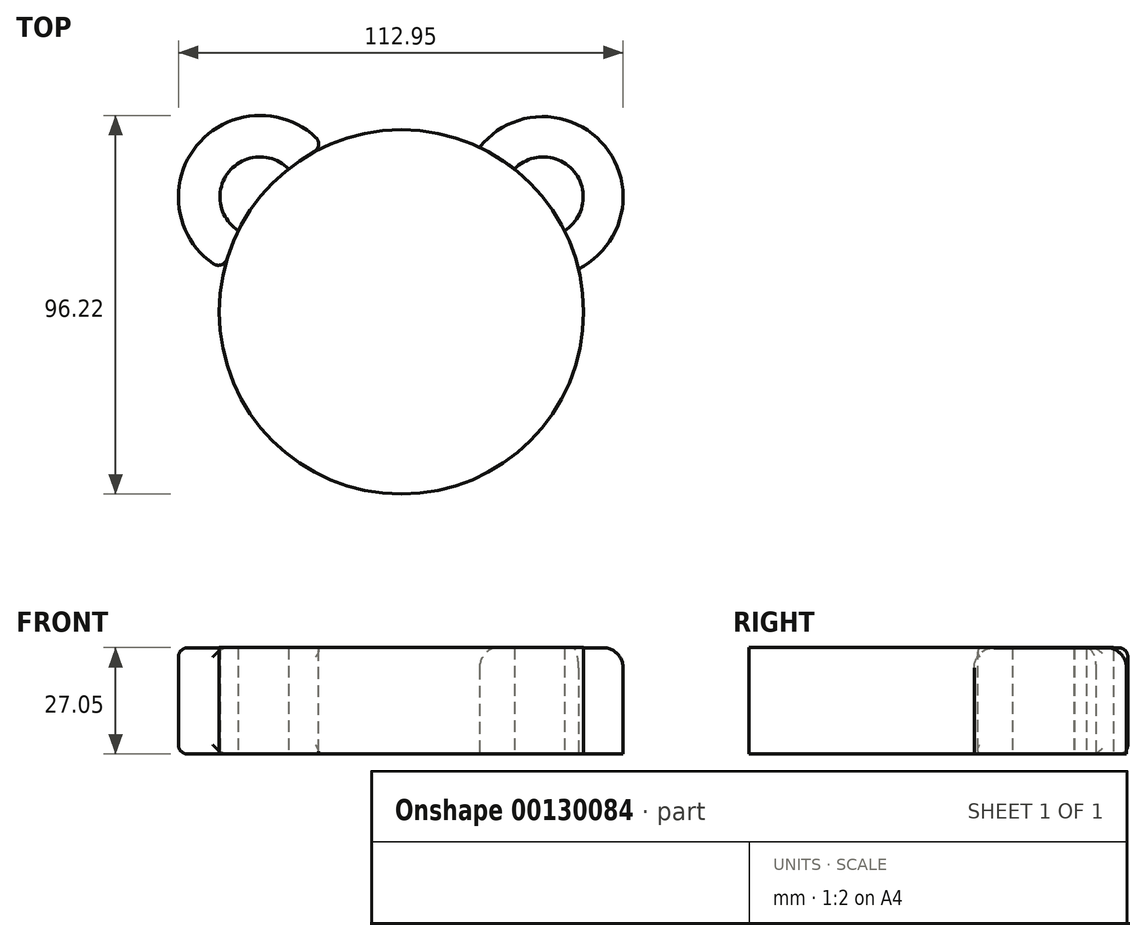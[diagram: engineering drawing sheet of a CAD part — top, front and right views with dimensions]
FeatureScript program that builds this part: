
annotation { "Feature Type Name" : "Feature", "Feature Type Description" : "" }
export const myFeature = defineFeature(function(context is Context, id is Id, definition is map)
    precondition{}
    {
        {
            var Q0;
            Q0=qCreatedBy(makeId("Top.planeOp"),FACE);
            var sketch = newSketch(context, id + "F0", { "sketchPlane" : qUnion([Q0])});
            skCircle(sketch, "E0", {"center": v(0, 0) * mm, "radius": 46.3 * mm});
            skArc(sketch, "E1", {"start": v(-19.58, 41.95) * mm, "mid": v(-51.99, 42.28) * mm, "end": v(-45.06, 10.62) * mm});
            skArc(sketch, "E2", {"start": v(44.98, 10.93) * mm, "mid": v(51.75, 42.09) * mm, "end": v(19.86, 41.81) * mm});
            skArc(sketch, "E3", {"start": v(-28.67, 36.35) * mm, "mid": v(-43.8, 35.62) * mm, "end": v(-41.42, 20.67) * mm});
            skArc(sketch, "E4", {"start": v(41.45, 20.61) * mm, "mid": v(43.92, 35.61) * mm, "end": v(28.73, 36.3) * mm});
            skSolve(sketch);
        }
        {
            var Q0;
            {var subQ0=sQuery(id+"F0.wireOp",EDGE,"E1");Q0=makeQuery(id+"F0.imprint","IMPRINT",FACE,{"disambiguationData":[TD([[makeQuery(id+"F0.imprint","IMPRINT",EDGE,{"derivedFrom":subQ0}),1.0]])]});}
            var Q1;
            {var subQ0=sQuery(id+"F0.wireOp",EDGE,"E2");Q1=makeQuery(id+"F0.imprint","IMPRINT",FACE,{"disambiguationData":[TD([[makeQuery(id+"F0.imprint","IMPRINT",EDGE,{"derivedFrom":subQ0}),1.0]])]});}
            extrude(context, id + "F1", {"entities" : qUnion([Q0, Q1]), "depth" : 27.02 * mm});
        }
        {
            var Q0;
            {var subQ1=sQuery(id+"F0.wireOp",EDGE,"E0");var subQ3=sQuery(id+"F0.wireOp",EDGE,"E2");var subQ8=makeQuery(id+"F0.imprint","INTERSECT",VERTEX,{"disambiguationData":[OD(0.0)],"derivedFrom":[subQ1,subQ3]});Q0=makeQuery(id+"F0.imprint","IMPRINT",FACE,{"disambiguationData":[TD([[makeQuery(id+"F0.imprint","IMPRINT",EDGE,{"disambiguationData":[TD([[subQ8,-1.0]])],"derivedFrom":subQ1}),1.0]])]});}
            extrude(context, id + "F2", {"entities" : qUnion([Q0]), "depth" : 27.05 * mm});
        }
        {
            var Q0;
            Q0=makeQuery(id+"F1.opExtrude","SWEPT_FACE",FACE,{"disambiguationData":[OSD([sQuery(id+"F0.wireOp",EDGE,"E1")])]});
            fillet(context, id + "F3", {"entities" : qUnion([Q0]), "radius" : 2.32 * mm, "tangentPropagation" : true, "allowEdgeOverflow" : false});
        }
        {
            var Q0;
            Q0=makeQuery(id+"F1.opExtrude","SWEPT_FACE",FACE,{"disambiguationData":[OSD([sQuery(id+"F0.wireOp",EDGE,"E1")])]});
            var Q1;
            Q1=makeQuery(id+"F1.opExtrude","CAP_EDGE",EDGE,{"disambiguationData":[OSD([sQuery(id+"F0.wireOp",EDGE,"E2")])],"isStart":false});
            fillet(context, id + "F4", {"entities" : qUnion([Q0, Q1]), "radius" : 5.08 * mm, "tangentPropagation" : true, "allowEdgeOverflow" : false});
        }
    });
